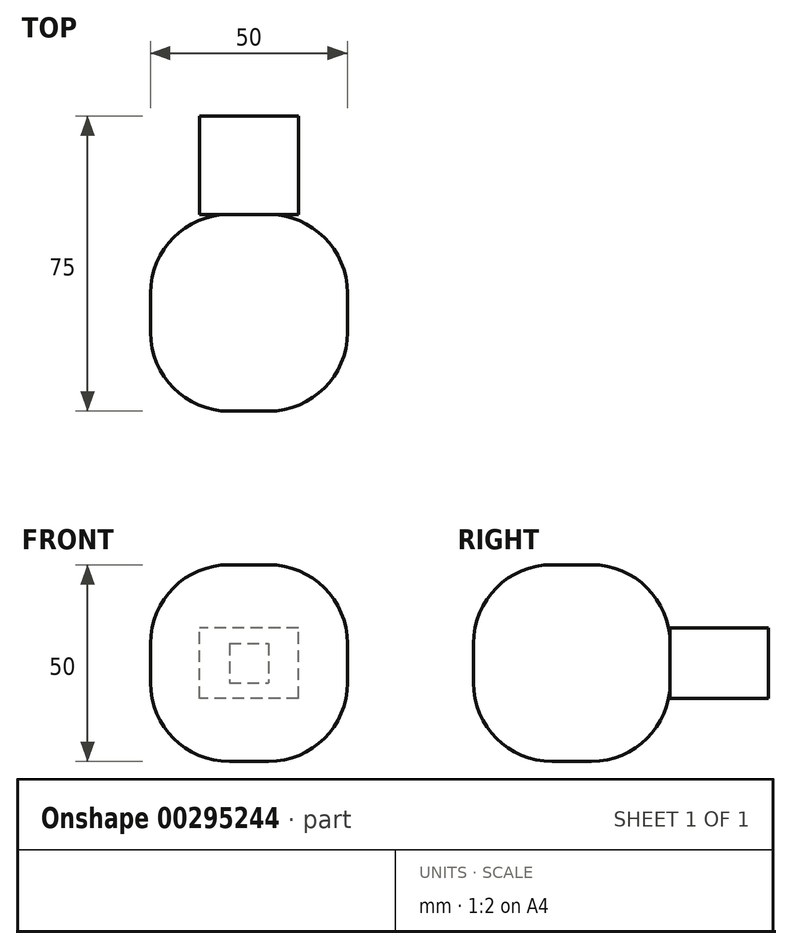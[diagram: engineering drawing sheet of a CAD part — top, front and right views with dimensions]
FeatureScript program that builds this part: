
annotation { "Feature Type Name" : "Feature", "Feature Type Description" : "" }
export const myFeature = defineFeature(function(context is Context, id is Id, definition is map)
    precondition{}
    {
        {
            var Q0;
            Q0=qCreatedBy(makeId("Front.planeOp"),FACE);
            var sketch = newSketch(context, id + "F0", { "sketchPlane" : qUnion([Q0])});
            skLineSegment(sketch, "E0.bottom", {"start": v(-25, 25) * mm, "end": v(25, 25) * mm});
            skLineSegment(sketch, "E0.top", {"start": v(-25, -25) * mm, "end": v(25, -25) * mm});
            skLineSegment(sketch, "E0.left", {"start": v(-25, 25) * mm, "end": v(-25, -25) * mm});
            skLineSegment(sketch, "E0.right", {"start": v(25, 25) * mm, "end": v(25, -25) * mm});
            skPoint(sketch, "E0.middle", {"position": v(0, 0) * mm});
            skSolve(sketch);
        }
        {
            var Q0;
            Q0 = qSketchRegion(id + "F0", true);
            extrude(context, id + "F1", {"entities" : qUnion([Q0]), "depth" : 50 * mm});
        }
        {
            var Q0;
            Q0=makeQuery(id+"F1.opExtrude","CAP_EDGE",EDGE,{"disambiguationData":[OSD([sQuery(id+"F0.wireOp",EDGE,"E0.right")])],"isStart":true});
            var Q1;
            Q1=makeQuery(id+"F1.opExtrude","CAP_EDGE",EDGE,{"disambiguationData":[OSD([sQuery(id+"F0.wireOp",EDGE,"E0.left")])],"isStart":true});
            var Q2;
            Q2=makeQuery(id+"F1.opExtrude","CAP_EDGE",EDGE,{"disambiguationData":[OSD([sQuery(id+"F0.wireOp",EDGE,"E0.right")])],"isStart":false});
            var Q3;
            Q3=makeQuery(id+"F1.opExtrude","SWEPT_FACE",FACE,{"disambiguationData":[OSD([sQuery(id+"F0.wireOp",EDGE,"E0.bottom")])]});
            var Q4;
            Q4=makeQuery(id+"F1.opExtrude","CAP_FACE",FACE,{"disambiguationData":[OSD([sQuery(id+"F0.wireOp",EDGE,"E0.bottom"),sQuery(id+"F0.wireOp",EDGE,"E0.top"),sQuery(id+"F0.wireOp",EDGE,"E0.left"),sQuery(id+"F0.wireOp",EDGE,"E0.right")])],"isStart":false});
            var Q5;
            Q5=makeQuery(id+"F1.opExtrude","SWEPT_EDGE",EDGE,{"disambiguationData":[OSD([sQuery(id+"F0.wireOp",EDGE,"E0.top"),sQuery(id+"F0.wireOp",EDGE,"E0.left")])]});
            var Q6;
            Q6=makeQuery(id+"F1.opExtrude","SWEPT_FACE",FACE,{"disambiguationData":[OSD([sQuery(id+"F0.wireOp",EDGE,"E0.left")])]});
            var Q7;
            Q7=makeQuery(id+"F1.opExtrude","CAP_EDGE",EDGE,{"disambiguationData":[OSD([sQuery(id+"F0.wireOp",EDGE,"E0.top")])],"isStart":true});
            var Q8;
            Q8=makeQuery(id+"F1.opExtrude","CAP_FACE",FACE,{"disambiguationData":[OSD([sQuery(id+"F0.wireOp",EDGE,"E0.bottom"),sQuery(id+"F0.wireOp",EDGE,"E0.top"),sQuery(id+"F0.wireOp",EDGE,"E0.left"),sQuery(id+"F0.wireOp",EDGE,"E0.right")])],"isStart":true});
            var Q9;
            Q9=makeQuery(id+"F1.opExtrude","SWEPT_EDGE",EDGE,{"disambiguationData":[OSD([sQuery(id+"F0.wireOp",EDGE,"E0.top"),sQuery(id+"F0.wireOp",EDGE,"E0.right")])]});
            fillet(context, id + "F2", {"entities" : qUnion([Q0, Q1, Q2, Q3, Q4, Q5, Q6, Q7, Q8, Q9]), "radius" : 20 * mm, "tangentPropagation" : true, "allowEdgeOverflow" : false});
        }
        {
            var Q0;
            Q0=qCreatedBy(makeId("Front.planeOp"),FACE);
            var sketch = newSketch(context, id + "F3", { "sketchPlane" : qUnion([Q0])});
            skLineSegment(sketch, "E1.bottom", {"start": v(12.6, -8.93) * mm, "end": v(-12.6, -8.93) * mm});
            skLineSegment(sketch, "E1.top", {"start": v(12.6, 8.93) * mm, "end": v(-12.6, 8.93) * mm});
            skLineSegment(sketch, "E1.left", {"start": v(12.6, -8.93) * mm, "end": v(12.6, 8.93) * mm});
            skLineSegment(sketch, "E1.right", {"start": v(-12.6, -8.93) * mm, "end": v(-12.6, 8.93) * mm});
            skPoint(sketch, "E1.middle", {"position": v(0, 0) * mm});
            skSolve(sketch);
        }
        {
            var Q0;
            Q0=makeQuery(id+"F3.imprint","IMPRINT",FACE,{"disambiguationData":[TD([[makeQuery(id+"F3.imprint","IMPRINT",EDGE,{"derivedFrom":sQuery(id+"F3.wireOp",EDGE,"E1.bottom")}),-1.0]])]});
            extrude(context, id + "F4", {"entities" : qUnion([Q0]), "operationType" : NewBodyOperationType.ADD, "oppositeDirection" : true, "depth" : 25 * mm});
        }
    });
